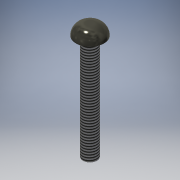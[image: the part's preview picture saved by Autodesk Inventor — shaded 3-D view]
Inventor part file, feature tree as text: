
AUTODESK INVENTOR PART (.ipt)
format: ipt  version: 2016 (Build 200138000, 138)  size: 133,120 bytes
history: native  units: mm
features: extrude x3, sketch x3, other x1, fillet x1, thread x1
ambient origin geometry x1: Origin
bodies: Body1 (feature_tree)
feature tree (9):
  other  "ソリッド1"
  extrude  "押し出し1"  Depth=4.0mm
  extrude  "押し出し2"  Depth=6.0mm TaperAngle=0.0deg
  fillet  "フィレット1"  Radius=8.0mm
  thread  "ねじ1"
  extrude  "押し出し3"  Depth=3.0mm TaperAngle=0.0deg
  sketch  "スケッチ1"
  sketch  "スケッチ2"
  sketch  "スケッチ3"
